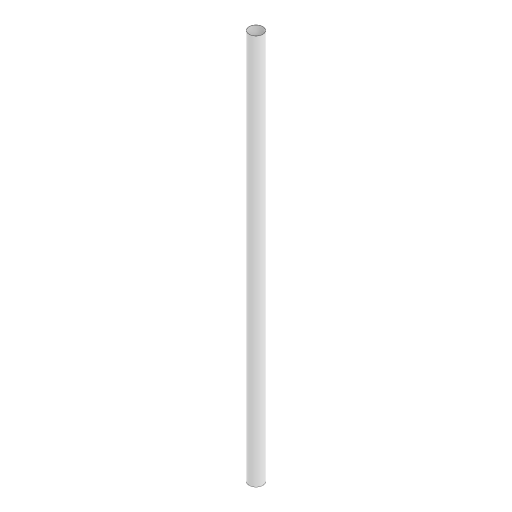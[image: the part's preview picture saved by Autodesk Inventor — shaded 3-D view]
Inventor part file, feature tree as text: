
AUTODESK INVENTOR PART (.ipt)
format: ipt  version: 2024.3 (Build 283343000, 343)  size: 82,944 bytes
history: native  units: mm
features: extrude x1, sketch x1
ambient origin geometry x8: Origin, YZ Plane, XZ Plane, XY Plane, X Axis, Y Axis, Z Axis, Center Point
bodies: Solid1 (feature_tree)
feature tree (2):
  extrude  "Extrusion1"  Depth=120.0mm
  sketch  "Sketch1"  dims[d0=4.1mm d1=4.2mm d2=120.0mm d3=0.0mm]
